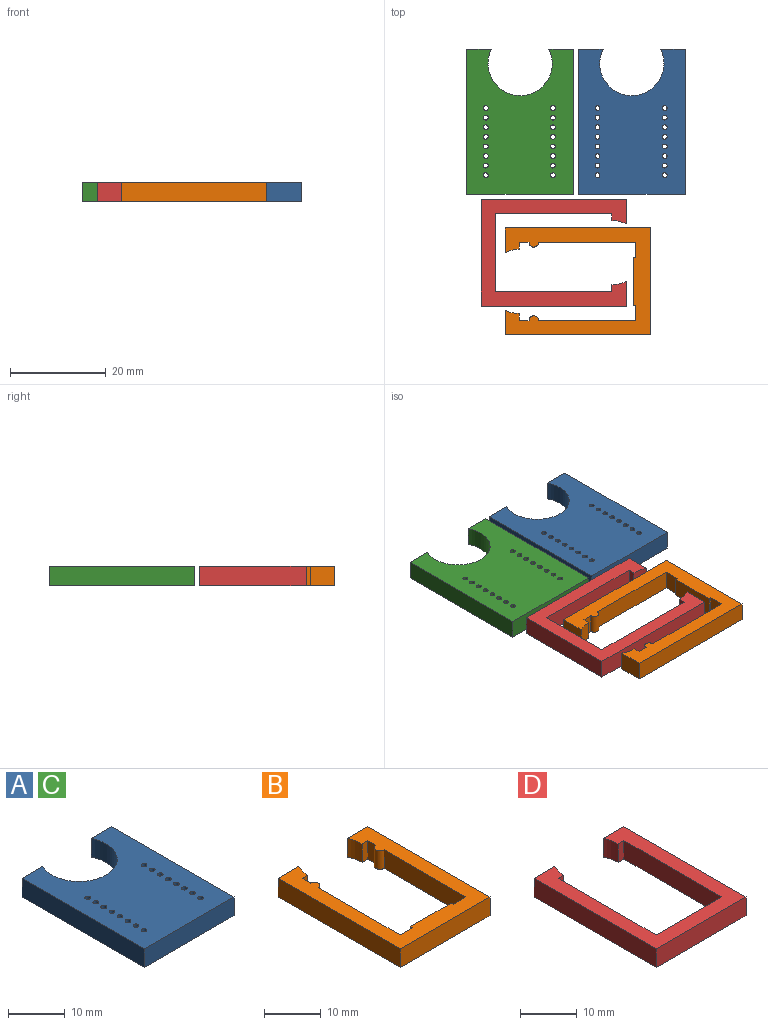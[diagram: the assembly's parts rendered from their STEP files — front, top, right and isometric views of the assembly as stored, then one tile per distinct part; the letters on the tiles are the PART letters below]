
ASSEMBLY  parts=4 mates=3
PART A: 24 faces, bbox 22.3x30.3x4 mm
  f0: plane 5.15x4mm, normal (0,1,0), area 20.6mm2, adj f1,f20,f22,f23
  f1: cylinder r=6.71mm len=13.42mm, axis (0,0,1), area 109.2mm2, adj f0,f2,f22,f23
  f2: plane 5.15x4mm, normal (0,1,0), area 20.6mm2, adj f1,f3,f22,f23
  f3: plane 30.3x4mm, normal (-1,0,0), area 121.2mm2, adj f2,f4,f22,f23
  f4: plane 22.3x4mm, normal (0,-1,0), area 89.2mm2, adj f3,f20,f22,f23
  f5: cylinder r=0.5mm len=4mm, axis (0,0,1), area 12.6mm2, adj f22,f23
  f6: cylinder r=0.5mm len=4mm, axis (0,0,1), area 12.6mm2, adj f22,f23
  f7: cylinder r=0.5mm len=4mm, axis (0,0,1), area 12.6mm2, adj f22,f23
  f8: cylinder r=0.5mm len=4mm, axis (0,0,1), area 12.6mm2, adj f22,f23
  f9: cylinder r=0.5mm len=4mm, axis (0,0,1), area 12.6mm2, adj f22,f23
  f10: cylinder r=0.5mm len=4mm, axis (0,0,1), area 12.6mm2, adj f22,f23
  f11: cylinder r=0.5mm len=4mm, axis (0,0,1), area 12.6mm2, adj f22,f23
  f12: cylinder r=0.5mm len=4mm, axis (0,0,1), area 12.6mm2, adj f22,f23
  f13: cylinder r=0.5mm len=4mm, axis (0,0,1), area 12.6mm2, adj f22,f23
  f14: cylinder r=0.5mm len=4mm, axis (0,0,1), area 12.6mm2, adj f22,f23
  f15: cylinder r=0.5mm len=4mm, axis (0,0,1), area 12.6mm2, adj f22,f23
  f16: cylinder r=0.5mm len=4mm, axis (0,0,1), area 12.6mm2, adj f22,f23
  f17: cylinder r=0.5mm len=4mm, axis (0,0,1), area 12.6mm2, adj f22,f23
  f18: cylinder r=0.5mm len=4mm, axis (0,0,1), area 12.6mm2, adj f22,f23
  f19: cylinder r=0.5mm len=4mm, axis (0,0,1), area 12.6mm2, adj f22,f23
  f20: plane 30.3x4mm, normal (1,0,0), area 121.2mm2, adj f0,f4,f22,f23
  f21: cylinder r=0.5mm len=4mm, axis (0,0,1), area 12.6mm2, adj f22,f23
  f22: plane 30.3x22.3mm, normal (0,0,-1), area 553.6mm2, adj f0,f1,f2,f3,f4,f5,f6,f7
  f23: plane 30.3x22.3mm, normal (0,0,1), area 553.6mm2, adj f0,f1,f2,f3,f4,f5,f6,f7
PART B: 22 faces, bbox 22.3x30.3x4 mm
  f0: plane 4x3.15mm, normal (0,1,0), area 12.6mm2, adj f1,f19,f20,f21
  f1: plane 4x0.5mm, normal (1,0,0), area 2mm2, adj f0,f2,f20,f21
  f2: plane 10x4mm, normal (0,1,0), area 40mm2, adj f1,f3,f20,f21
  f3: plane 4x0.5mm, normal (-1,0,0), area 2mm2, adj f2,f4,f20,f21
  f4: plane 4x3.15mm, normal (0,1,0), area 12.6mm2, adj f3,f5,f20,f21
  f5: plane 20.3x4mm, normal (1,0,0), area 81.2mm2, adj f4,f6,f20,f21
  f6: cylinder r=1mm len=4mm, axis (0,0,-1), area 12.6mm2, adj f5,f7,f20,f21
  f7: plane 4x2mm, normal (1,0,0), area 8mm2, adj f6,f8,f20,f21
  f8: plane 4x1.44mm, normal (0,-1,0), area 5.8mm2, adj f7,f9,f20,f21
  f9: cylinder r=6.71mm len=4mm, axis (0,0,-1), area 12.4mm2, adj f8,f10,f20,f21
  f10: plane 5.15x4mm, normal (0,1,0), area 20.6mm2, adj f9,f11,f20,f21
  f11: plane 30.3x4mm, normal (-1,0,0), area 121.2mm2, adj f10,f12,f20,f21
  f12: plane 22.3x4mm, normal (0,-1,0), area 89.2mm2, adj f11,f13,f20,f21
  f13: plane 30.3x4mm, normal (1,0,0), area 121.2mm2, adj f12,f14,f20,f21
  f14: plane 5.15x4mm, normal (0,1,0), area 20.6mm2, adj f13,f15,f20,f21
  f15: cylinder r=6.71mm len=4mm, axis (0,0,-1), area 12.4mm2, adj f14,f16,f20,f21
  f16: plane 4x1.44mm, normal (0,-1,0), area 5.8mm2, adj f15,f17,f20,f21
  f17: plane 4x2mm, normal (-1,0,0), area 8mm2, adj f16,f18,f20,f21
  f18: cylinder r=1mm len=4mm, axis (0,0,-1), area 12.6mm2, adj f17,f19,f20,f21
  f19: plane 20.3x4mm, normal (-1,0,0), area 81.2mm2, adj f0,f18,f20,f21
  f20: plane 30.3x22.3mm, normal (0,0,1), area 248.9mm2, adj f0,f1,f2,f3,f4,f5,f6,f7
  f21: plane 30.3x22.3mm, normal (0,0,-1), area 248.9mm2, adj f0,f1,f2,f3,f4,f5,f6,f7
PART C: same geometry as A
PART D: 14 faces, bbox 22.3x30.3x4 mm
  f0: plane 16.3x4mm, normal (0,1,0), area 65.2mm2, adj f1,f11,f12,f13
  f1: plane 24.3x4mm, normal (1,0,0), area 97.2mm2, adj f0,f2,f12,f13
  f2: plane 4x1.44mm, normal (0,-1,0), area 5.8mm2, adj f1,f3,f12,f13
  f3: cylinder r=6.71mm len=4mm, axis (0,0,-1), area 12.4mm2, adj f2,f4,f12,f13
  f4: plane 5.15x4mm, normal (0,1,0), area 20.6mm2, adj f3,f5,f12,f13
  f5: plane 30.3x4mm, normal (-1,0,0), area 121.2mm2, adj f4,f6,f12,f13
  f6: plane 22.3x4mm, normal (0,-1,0), area 89.2mm2, adj f5,f7,f12,f13
  f7: plane 30.3x4mm, normal (1,0,0), area 121.2mm2, adj f6,f8,f12,f13
  f8: plane 5.15x4mm, normal (0,1,0), area 20.6mm2, adj f7,f9,f12,f13
  f9: cylinder r=6.71mm len=4mm, axis (0,0,-1), area 12.4mm2, adj f8,f10,f12,f13
  f10: plane 4x1.44mm, normal (0,-1,0), area 5.8mm2, adj f9,f11,f12,f13
  f11: plane 24.3x4mm, normal (-1,0,0), area 97.2mm2, adj f0,f10,f12,f13
  f12: plane 30.3x22.3mm, normal (0,0,1), area 240.7mm2, adj f0,f1,f2,f3,f4,f5,f6,f7
  f13: plane 30.3x22.3mm, normal (0,0,-1), area 240.7mm2, adj f0,f1,f2,f3,f4,f5,f6,f7
PLACE A t=(11.15,3.25,-2.95)mm
PLACE B rot(axis=(0,0,1),90deg) t=(-0.15,-30.05,-10.95)mm
PLACE C t=(-12.15,3.25,-2.95)mm
PLACE D rot(axis=(0,0,-1),90deg) t=(-5.15,-24.05,-6.95)mm
MATE fastened C.f23 <-> A.f23  axis (0,0,1) through (-1,18.4,-2.95)mm
MATE fastened D.f12 <-> C.f23  axis (0,0,1) through (-20.3,-12.9,-2.95)mm
MATE fastened B.f20 <-> D.f12  axis (0,0,1) through (15,-41.2,-2.95)mm
